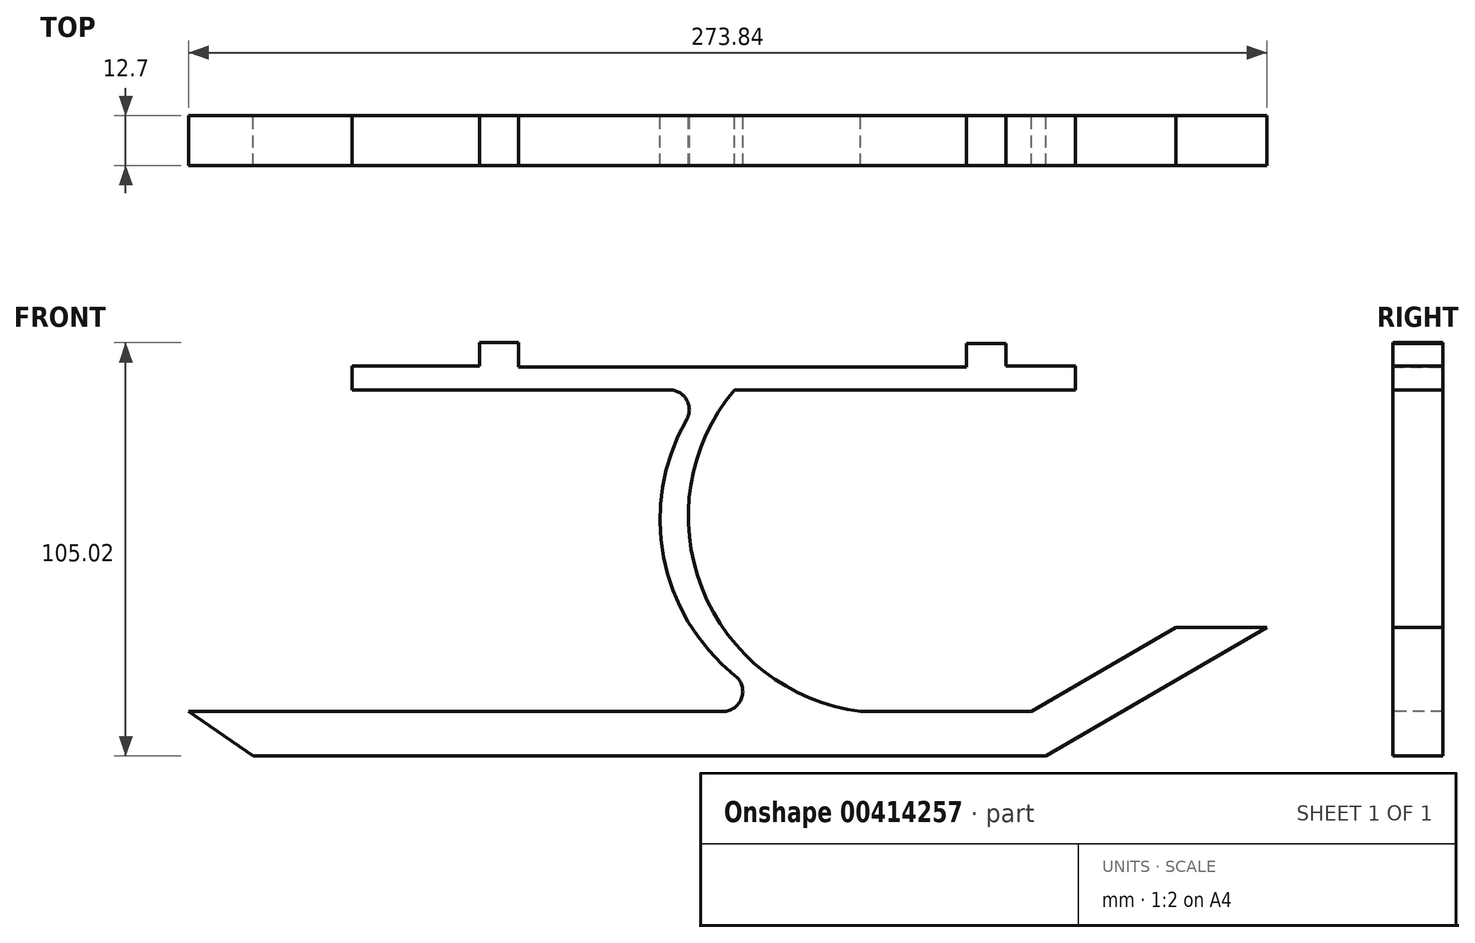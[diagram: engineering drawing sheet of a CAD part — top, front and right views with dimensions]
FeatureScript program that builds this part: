
annotation { "Feature Type Name" : "Feature", "Feature Type Description" : "" }
export const myFeature = defineFeature(function(context is Context, id is Id, definition is map)
    precondition{}
    {
        {
            var Q0;
            Q0=qCreatedBy(makeId("Front.planeOp"),FACE);
            var sketch = newSketch(context, id + "F0", { "sketchPlane" : qUnion([Q0])});
            skLineSegment(sketch, "E0", {"start": v(-117.37, -60.3) * mm, "end": v(84.1, -60.3) * mm});
            skLineSegment(sketch, "E1", {"start": v(84.1, -60.3) * mm, "end": v(140.15, -27.65) * mm});
            skLineSegment(sketch, "E2", {"start": v(140.15, -27.65) * mm, "end": v(117.05, -27.65) * mm});
            skLineSegment(sketch, "E3", {"start": v(117.05, -27.65) * mm, "end": v(80.44, -48.98) * mm});
            skLineSegment(sketch, "E4", {"start": v(80.44, -48.98) * mm, "end": v(36.96, -48.98) * mm});
            skLineSegment(sketch, "E5", {"start": v(-133.7, -48.98) * mm, "end": v(-117.37, -60.3) * mm});
            skArc(sketch, "E6", {"start": v(4.92, 32.72) * mm, "mid": v(-3.35, -17.65) * mm, "end": v(36.96, -48.98) * mm});
            skLineSegment(sketch, "E7", {"start": v(-1.85, 32.72) * mm, "end": v(-92.17, 32.72) * mm});
            skLineSegment(sketch, "E8", {"start": v(-92.17, 32.72) * mm, "end": v(-92.17, 38.72) * mm});
            skLineSegment(sketch, "E9", {"start": v(-92.17, 38.72) * mm, "end": v(-59.87, 38.72) * mm});
            skLineSegment(sketch, "E10", {"start": v(-59.87, 38.72) * mm, "end": v(-59.87, 44.72) * mm});
            skLineSegment(sketch, "E11", {"start": v(-59.87, 44.72) * mm, "end": v(-49.87, 44.72) * mm});
            skLineSegment(sketch, "E12", {"start": v(-49.87, 44.72) * mm, "end": v(-49.87, 38.5) * mm});
            skLineSegment(sketch, "E13", {"start": v(-49.87, 38.5) * mm, "end": v(63.9, 38.5) * mm});
            skLineSegment(sketch, "E14", {"start": v(63.9, 38.5) * mm, "end": v(63.9, 44.5) * mm});
            skLineSegment(sketch, "E15", {"start": v(63.9, 44.5) * mm, "end": v(73.9, 44.5) * mm});
            skLineSegment(sketch, "E16", {"start": v(73.9, 44.5) * mm, "end": v(73.9, 38.72) * mm});
            skLineSegment(sketch, "E17", {"start": v(73.9, 38.72) * mm, "end": v(91.52, 38.72) * mm});
            skLineSegment(sketch, "E18", {"start": v(91.52, 38.72) * mm, "end": v(91.52, 32.72) * mm});
            skLineSegment(sketch, "E19", {"start": v(91.52, 32.72) * mm, "end": v(4.92, 32.72) * mm});
            skArc(sketch, "E20", {"start": v(-1.85, 32.72) * mm, "mid": v(-11.86, -14.77) * mm, "end": v(22.58, -48.98) * mm});
            skLineSegment(sketch, "E21.trimOffspring", {"start": v(22.58, -48.98) * mm, "end": v(-133.7, -48.98) * mm});
            skSolve(sketch);
        }
        {
            var Q0;
            {var subQ0=sQuery(id+"F0.wireOp",EDGE,"E6");Q0=makeQuery(id+"F0.imprint","IMPRINT",FACE,{"disambiguationData":[TD([[makeQuery(id+"F0.imprint","IMPRINT",EDGE,{"derivedFrom":subQ0}),-1.0]])]});}
            var Q1;
            Q1=makeQuery(id+"F0.imprint","IMPRINT",FACE,{"disambiguationData":[TD([[makeQuery(id+"F0.imprint","IMPRINT",EDGE,{"derivedFrom":sQuery(id+"F0.wireOp",EDGE,"E0")}),1.0]])]});
            extrude(context, id + "F1", {"entities" : qUnion([Q0, Q1]), "endBound" : BoundingType.SYMMETRIC, "depth" : 12.7 * mm});
        }
        {
            var Q0;
            Q0=makeQuery(id+"F1.opExtrude","SWEPT_EDGE",EDGE,{"disambiguationData":[OSD([sQuery(id+"F0.wireOp",EDGE,"E20"),sQuery(id+"F0.wireOp",EDGE,"E21.trimOffspring")])]});
            var Q1;
            Q1=makeQuery(id+"F1.opExtrude","SWEPT_EDGE",EDGE,{"disambiguationData":[OSD([sQuery(id+"F0.wireOp",EDGE,"E7"),sQuery(id+"F0.wireOp",EDGE,"E20")])]});
            fillet(context, id + "F2", {"entities" : qUnion([Q0, Q1]), "radius" : 5.08 * mm, "tangentPropagation" : true, "allowEdgeOverflow" : false});
        }
    });
